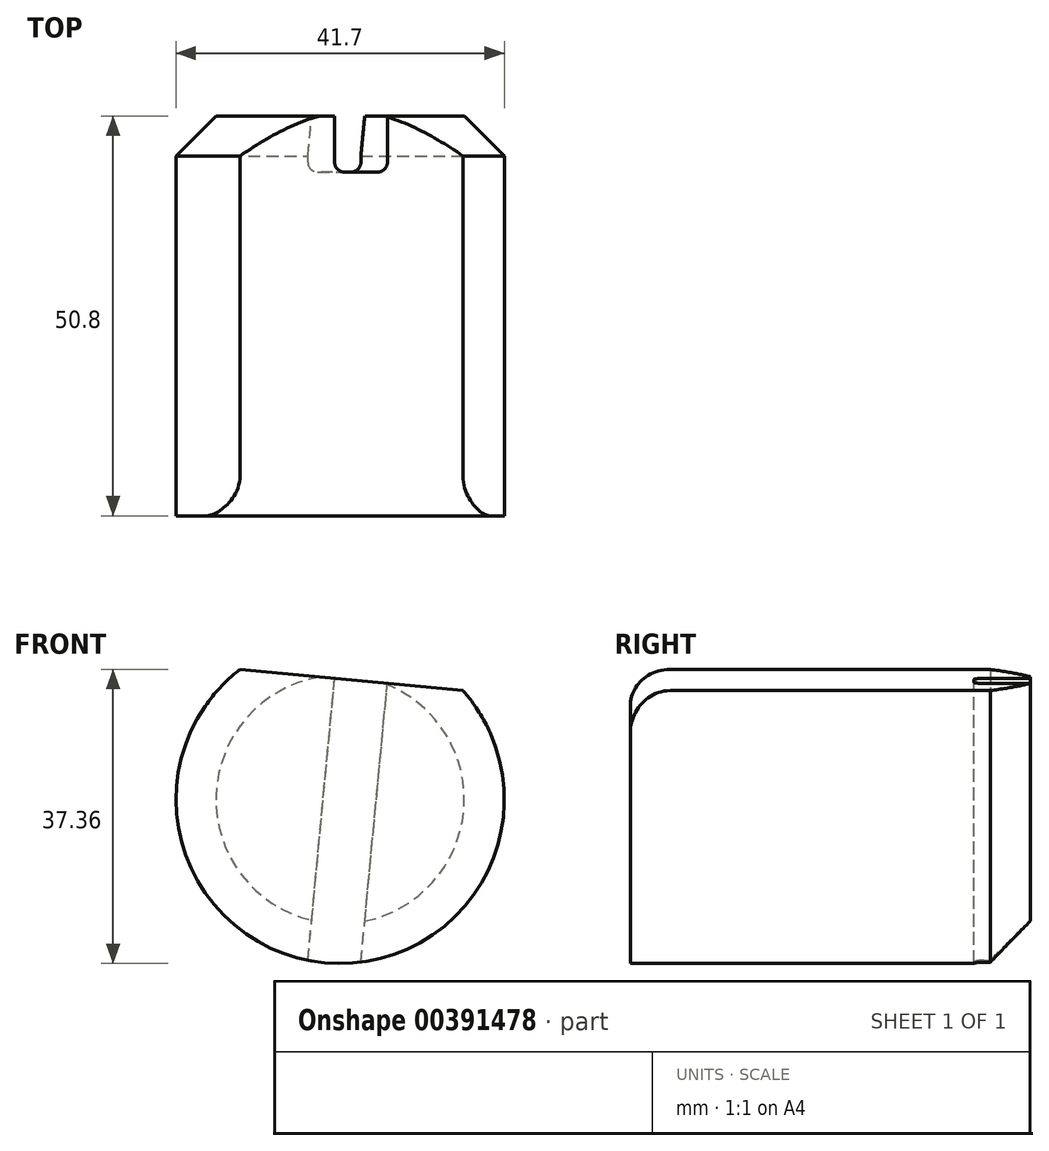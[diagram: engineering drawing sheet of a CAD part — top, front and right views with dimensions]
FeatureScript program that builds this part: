
annotation { "Feature Type Name" : "Feature", "Feature Type Description" : "" }
export const myFeature = defineFeature(function(context is Context, id is Id, definition is map)
    precondition{}
    {
        {
            var Q0;
            Q0=qCreatedBy(makeId("Front.planeOp"),FACE);
            cPlane(context, id + "F0", {"entities" : qUnion([Q0]), "cplaneType" : CPlaneType.OFFSET, "offset" : 141.48 * mm, "width" : 152.4 * mm, "height" : 152.4 * mm});
        }
        {
            var Q0;
            Q0=qCreatedBy(makeId("Front.planeOp"),FACE);
            var sketch = newSketch(context, id + "F1", { "sketchPlane" : qUnion([Q0])});
            skLineSegment(sketch, "E0", {"start": v(0, 0) * mm, "end": v(-127, 46.33) * mm});
            skSolve(sketch);
        }
        {
            var Q0;
            Q0=qCreatedBy(id+"F0.planeOp",FACE);
            var sketch = newSketch(context, id + "F2", { "sketchPlane" : qUnion([Q0])});
            skArc(sketch, "E1", {"start": v(-139.72, 62.85) * mm, "mid": v(-128.97, 25.58) * mm, "end": v(-111.4, 60.16) * mm});
            skLineSegment(sketch, "E2", {"start": v(-139.72, 62.85) * mm, "end": v(-111.4, 60.16) * mm});
            skSolve(sketch);
        }
        {
            var Q0;
            Q0=makeQuery(id+"F2.imprint","IMPRINT",FACE,{"disambiguationData":[TD([[makeQuery(id+"F2.imprint","IMPRINT",EDGE,{"derivedFrom":sQuery(id+"F2.wireOp",EDGE,"E1")}),1.0]])]});
            extrude(context, id + "F3", {"entities" : qUnion([Q0]), "depth" : 50.8 * mm});
        }
        {
            var Q0;
            Q0=makeQuery(id+"F3.opExtrude","CAP_EDGE",EDGE,{"disambiguationData":[OSD([sQuery(id+"F2.wireOp",EDGE,"E2")])],"isStart":false});
            fillet(context, id + "F4", {"entities" : qUnion([Q0]), "radius" : 5.08 * mm, "tangentPropagation" : true, "allowEdgeOverflow" : false});
        }
        {
            var Q0;
            Q0=makeQuery(id+"F3.opExtrude","CAP_EDGE",EDGE,{"disambiguationData":[OSD([sQuery(id+"F2.wireOp",EDGE,"E1")])],"isStart":true});
            chamfer(context, id + "F5", {"entities" : qUnion([Q0]), "width" : 5.08 * mm, "tangentPropagation" : true});
        }
        {
            var Q0;
            Q0=makeQuery(id+"F3.opExtrude","SWEPT_FACE",FACE,{"disambiguationData":[OSD([sQuery(id+"F2.wireOp",EDGE,"E2")])]});
            var sketch = newSketch(context, id + "F6", { "sketchPlane" : qUnion([Q0])});
            skSolve(sketch);
        }
        {
            var Q0;
            {var subQ0=sQuery(id+"F2.wireOp",EDGE,"E2");Q0=makeQuery(id+"F6.imprint","IMPRINT",FACE,{"disambiguationData":[TD([[makeQuery(id+"F6.imprint","IMPRINT",EDGE,{"derivedFrom":makeQuery(id+"F3.opExtrude","CAP_EDGE",EDGE,{"disambiguationData":[OSD([subQ0])],"isStart":true})}),-1.0]])]});}
            var sketch = newSketch(context, id + "F7", { "sketchPlane" : qUnion([Q0])});
            skLineSegment(sketch, "E3.bottom", {"start": v(-126.24, -141.48) * mm, "end": v(-132.96, -141.48) * mm});
            skLineSegment(sketch, "E3.top", {"start": v(-126.24, -148.61) * mm, "end": v(-132.96, -148.61) * mm});
            skLineSegment(sketch, "E3.left", {"start": v(-126.24, -141.48) * mm, "end": v(-126.24, -148.61) * mm});
            skLineSegment(sketch, "E3.right", {"start": v(-132.96, -141.48) * mm, "end": v(-132.96, -148.61) * mm});
            skSolve(sketch);
        }
        {
            var Q0;
            Q0 = qSketchRegion(id + "F7", true);
            extrude(context, id + "F8", {"entities" : qUnion([Q0]), "operationType" : NewBodyOperationType.REMOVE, "oppositeDirection" : true, "depth" : 50.8 * mm});
        }
        {
            var Q0;
            Q0=makeQuery(id+"F8.boolean.opBoolean","COPY",EDGE,{"derivedFrom":makeQuery(id+"F8.opExtrude","SWEPT_EDGE",EDGE,{"disambiguationData":[OSD([sQuery(id+"F7.wireOp",EDGE,"E3.top"),sQuery(id+"F7.wireOp",EDGE,"E3.right")])]})});
            var Q1;
            Q1=makeQuery(id+"F8.boolean.opBoolean","COPY",EDGE,{"derivedFrom":makeQuery(id+"F8.opExtrude","SWEPT_EDGE",EDGE,{"disambiguationData":[OSD([sQuery(id+"F7.wireOp",EDGE,"E3.top"),sQuery(id+"F7.wireOp",EDGE,"E3.left")])]})});
            fillet(context, id + "F9", {"entities" : qUnion([Q0, Q1]), "radius" : 1.27 * mm, "tangentPropagation" : true, "allowEdgeOverflow" : false});
        }
    });
